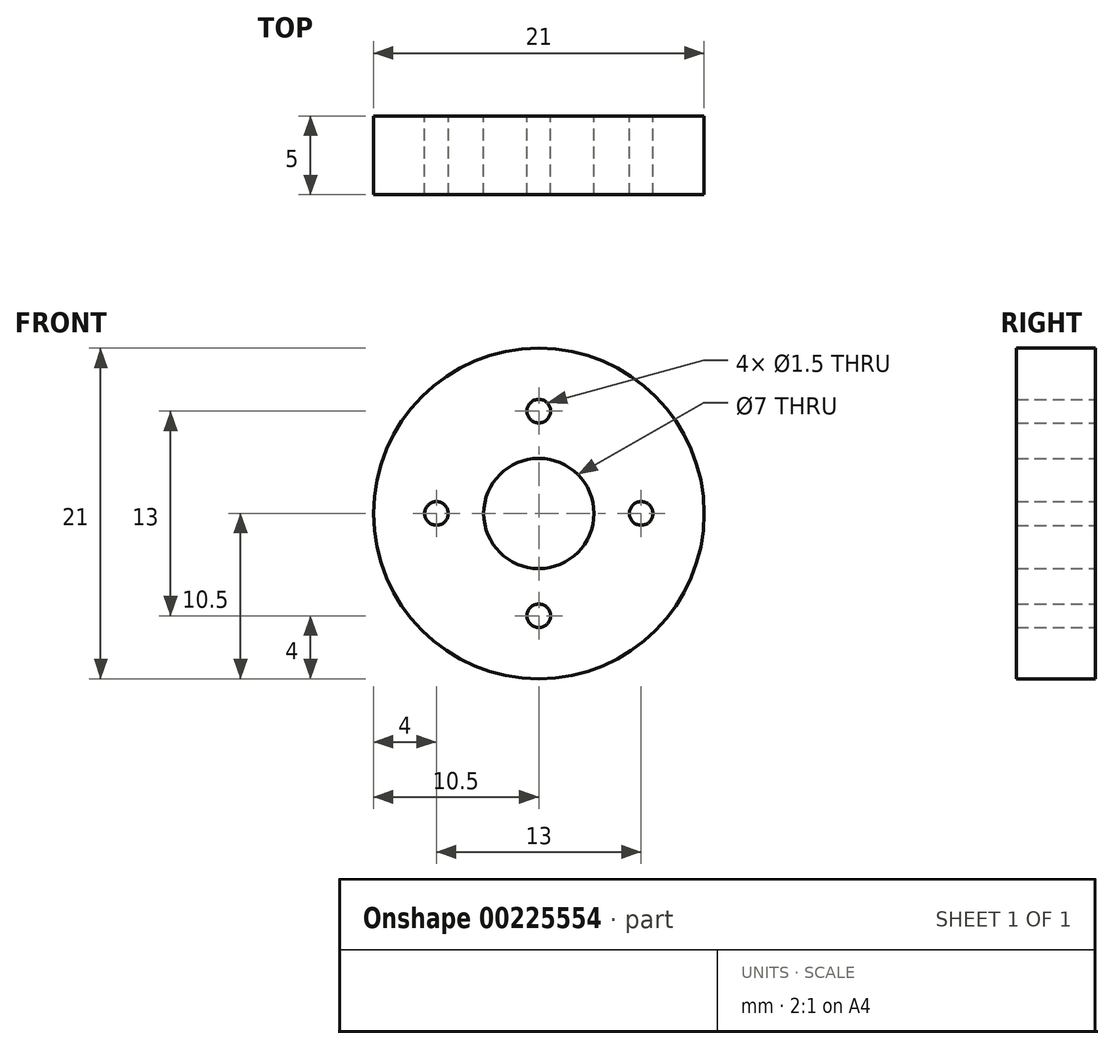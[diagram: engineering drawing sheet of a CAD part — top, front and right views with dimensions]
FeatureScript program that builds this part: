
annotation { "Feature Type Name" : "Feature", "Feature Type Description" : "" }
export const myFeature = defineFeature(function(context is Context, id is Id, definition is map)
    precondition{}
    {
        {
            var Q0;
            Q0=qCreatedBy(makeId("Front.planeOp"),FACE);
            var sketch = newSketch(context, id + "F0", { "sketchPlane" : qUnion([Q0])});
            skCircle(sketch, "E0", {"center": v(0, 0) * mm, "radius": 3.5 * mm});
            skCircle(sketch, "E1", {"center": v(0, 0) * mm, "radius": 10.5 * mm});
            skLineSegment(sketch, "E2", {"start": v(0, 10.5) * mm, "end": v(0, -10.5) * mm, "construction": true});
            skLineSegment(sketch, "E3", {"start": v(-10.5, 0) * mm, "end": v(10.5, 0) * mm, "construction": true});
            skCircle(sketch, "E4", {"center": v(6.5, 0) * mm, "radius": 0.75 * mm});
            skCircle(sketch, "E5.1.0", {"center": v(0, -6.5) * mm, "radius": 0.75 * mm});
            skCircle(sketch, "E5.2.0", {"center": v(-6.5, 0) * mm, "radius": 0.75 * mm});
            skCircle(sketch, "E5.3.0", {"center": v(0, 6.5) * mm, "radius": 0.75 * mm});
            skLineSegment(sketch, "E5.anchor1", {"start": v(0, 0) * mm, "end": v(6.5, 0) * mm, "construction": true});
            skLineSegment(sketch, "E5.anchor2", {"start": v(0, 0) * mm, "end": v(0, 6.5) * mm, "construction": true});
            skSolve(sketch);
        }
        {
            var Q0;
            Q0=makeQuery(id+"F0.imprint","IMPRINT",FACE,{"disambiguationData":[TD([[makeQuery(id+"F0.imprint","IMPRINT",EDGE,{"derivedFrom":sQuery(id+"F0.wireOp",EDGE,"E0")}),-1.0]])]});
            extrude(context, id + "F1", {"entities" : qUnion([Q0]), "depth" : 5 * mm});
        }
    });
